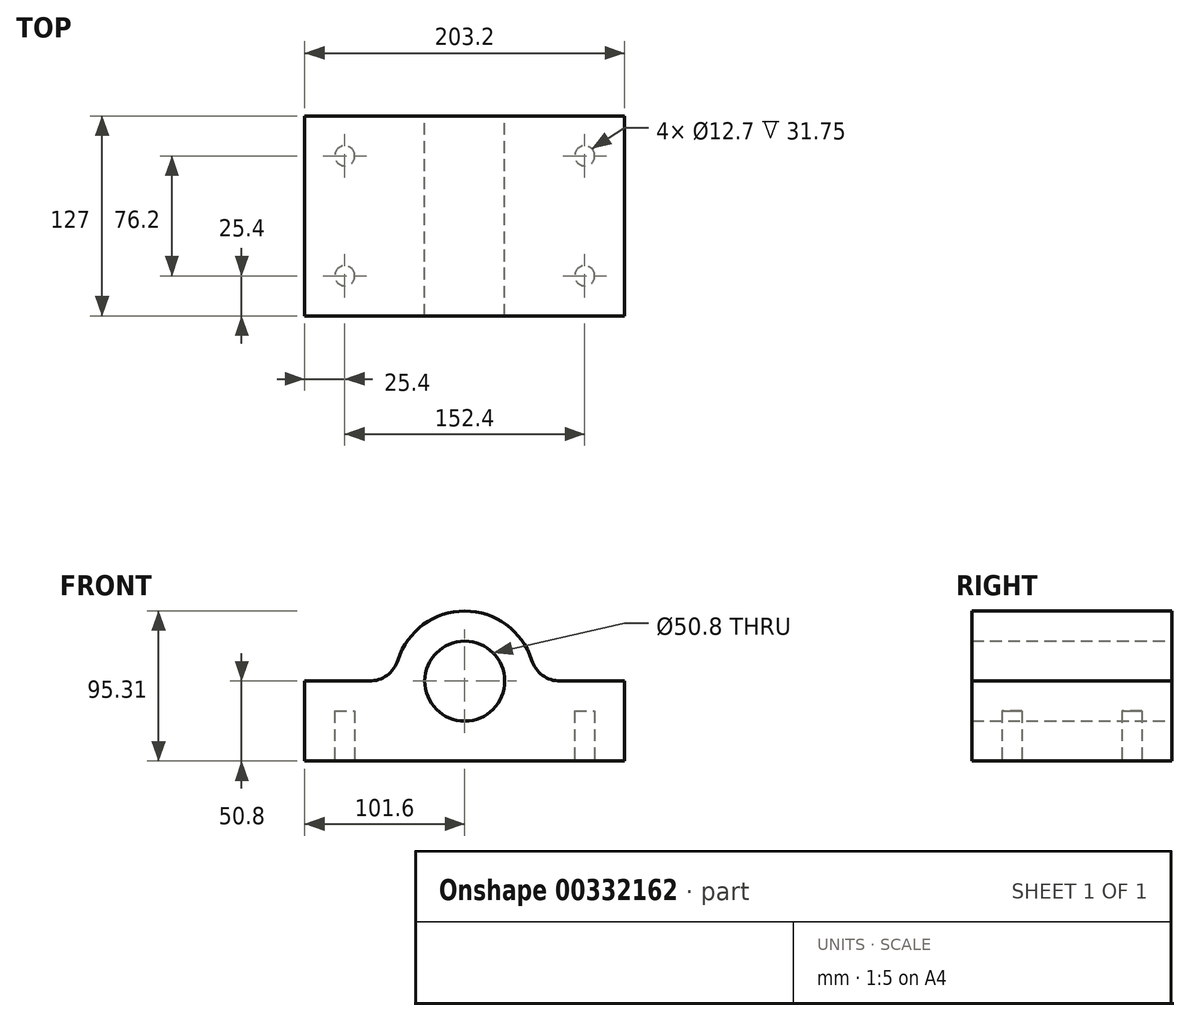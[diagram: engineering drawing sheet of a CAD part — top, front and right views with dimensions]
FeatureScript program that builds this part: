
annotation { "Feature Type Name" : "Feature", "Feature Type Description" : "" }
export const myFeature = defineFeature(function(context is Context, id is Id, definition is map)
    precondition{}
    {
        {
            var Q0;
            Q0=qCreatedBy(makeId("Front.planeOp"),FACE);
            var sketch = newSketch(context, id + "F0", { "sketchPlane" : qUnion([Q0])});
            skCircle(sketch, "E0", {"center": v(0, 0) * mm, "radius": 25.4 * mm});
            skArc(sketch, "E1", {"start": v(42.46, 13.34) * mm, "mid": v(0, 44.5) * mm, "end": v(-42.46, 13.34) * mm});
            skLineSegment(sketch, "E2", {"start": v(0, 0) * mm, "end": v(25.4, 0) * mm});
            skLineSegment(sketch, "E3", {"start": v(101.6, 0) * mm, "end": v(101.6, -50.8) * mm});
            skLineSegment(sketch, "E4", {"start": v(101.6, -50.8) * mm, "end": v(-101.6, -50.8) * mm});
            skLineSegment(sketch, "E5", {"start": v(-101.6, -50.8) * mm, "end": v(-101.6, 0) * mm});
            skLineSegment(sketch, "E6", {"start": v(-101.6, 0) * mm, "end": v(-60.63, 0) * mm});
            skArc(sketch, "E7", {"start": v(-60.63, 0) * mm, "mid": v(-49.36, 3.7) * mm, "end": v(-42.46, 13.34) * mm});
            skArc(sketch, "E8", {"start": v(42.46, 13.34) * mm, "mid": v(49.36, 3.7) * mm, "end": v(60.63, 0) * mm});
            skLineSegment(sketch, "E9.trimOffspring", {"start": v(-25.4, 0) * mm, "end": v(0, 0) * mm});
            skLineSegment(sketch, "E10.trimOffspring", {"start": v(60.63, 0) * mm, "end": v(101.6, 0) * mm});
            skSolve(sketch);
        }
        {
            var Q0;
            Q0 = qSketchRegion(id + "F0", true);
            extrude(context, id + "F1", {"entities" : qUnion([Q0]), "depth" : 127 * mm});
        }
        {
            var Q0;
            Q0=makeQuery(id+"F1.opExtrude","SWEPT_FACE",FACE,{"disambiguationData":[OSD([sQuery(id+"F0.wireOp",EDGE,"E4")])]});
            var sketch = newSketch(context, id + "F2", { "sketchPlane" : qUnion([Q0])});
            skCircle(sketch, "E11", {"center": v(76.2, 101.6) * mm, "radius": 6.35 * mm});
            skCircle(sketch, "E12", {"center": v(76.2, 25.4) * mm, "radius": 6.35 * mm});
            skCircle(sketch, "E13", {"center": v(-76.2, 101.6) * mm, "radius": 6.35 * mm});
            skCircle(sketch, "E14", {"center": v(-76.2, 25.4) * mm, "radius": 6.35 * mm});
            skSolve(sketch);
        }
        {
            var Q0;
            Q0=makeQuery(id+"F2.imprint","IMPRINT",FACE,{"disambiguationData":[TD([[makeQuery(id+"F2.imprint","IMPRINT",EDGE,{"derivedFrom":sQuery(id+"F2.wireOp",EDGE,"E13")}),1.0]])]});
            var Q1;
            Q1=makeQuery(id+"F2.imprint","IMPRINT",FACE,{"disambiguationData":[TD([[makeQuery(id+"F2.imprint","IMPRINT",EDGE,{"derivedFrom":sQuery(id+"F2.wireOp",EDGE,"E14")}),1.0]])]});
            var Q2;
            Q2=makeQuery(id+"F2.imprint","IMPRINT",FACE,{"disambiguationData":[TD([[makeQuery(id+"F2.imprint","IMPRINT",EDGE,{"derivedFrom":sQuery(id+"F2.wireOp",EDGE,"E12")}),1.0]])]});
            var Q3;
            Q3=makeQuery(id+"F2.imprint","IMPRINT",FACE,{"disambiguationData":[TD([[makeQuery(id+"F2.imprint","IMPRINT",EDGE,{"derivedFrom":sQuery(id+"F2.wireOp",EDGE,"E11")}),1.0]])]});
            extrude(context, id + "F3", {"entities" : qUnion([Q0, Q1, Q2, Q3]), "operationType" : NewBodyOperationType.REMOVE, "oppositeDirection" : true, "depth" : 31.75 * mm});
        }
    });
